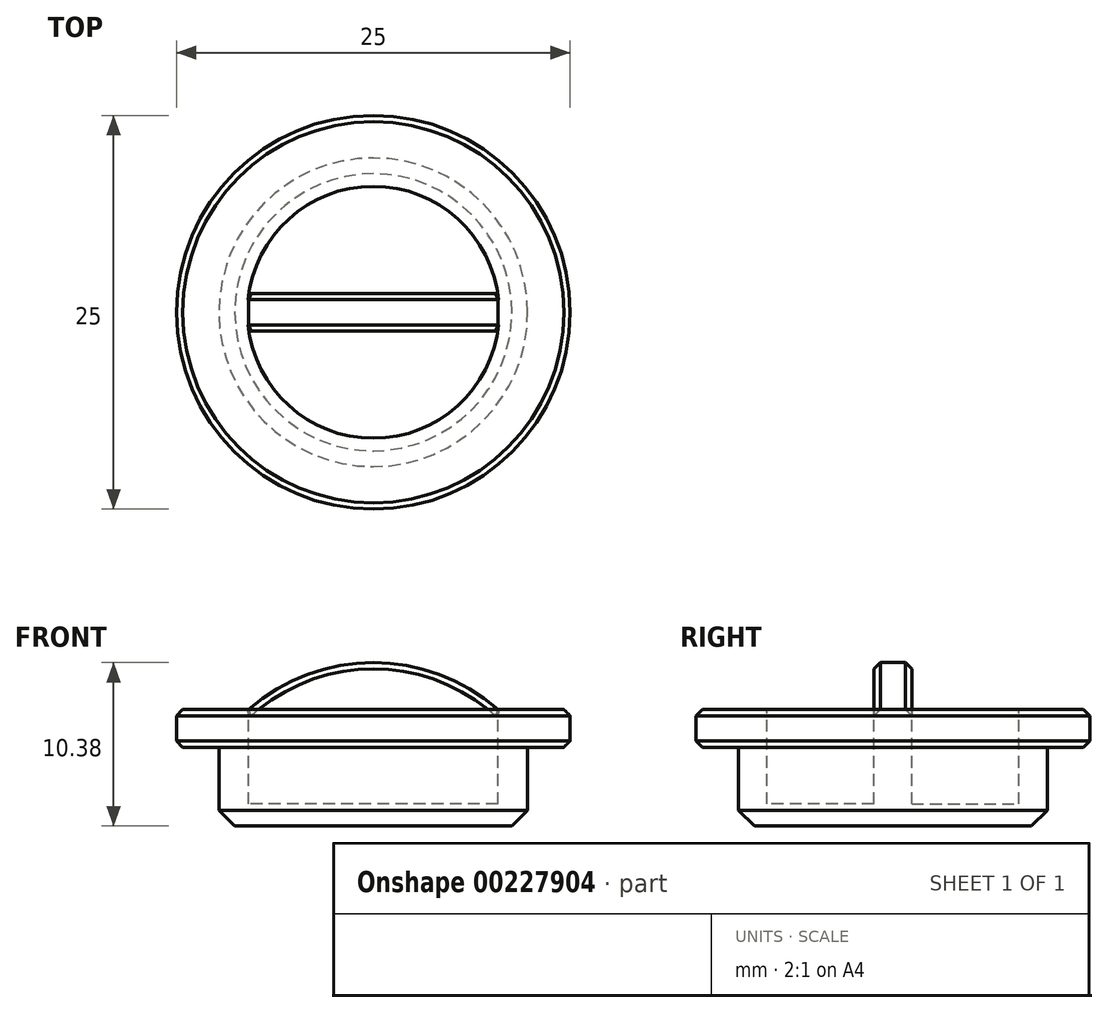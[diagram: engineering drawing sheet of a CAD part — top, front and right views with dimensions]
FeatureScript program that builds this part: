
annotation { "Feature Type Name" : "Feature", "Feature Type Description" : "" }
export const myFeature = defineFeature(function(context is Context, id is Id, definition is map)
    precondition{}
    {
        {
            var Q0;
            Q0=qCreatedBy(makeId("Top.planeOp"),FACE);
            var sketch = newSketch(context, id + "F0", { "sketchPlane" : qUnion([Q0])});
            skCircle(sketch, "E0", {"center": v(0, 0) * mm, "radius": 9.8 * mm});
            skSolve(sketch);
        }
        {
            var Q0;
            Q0=makeQuery(id+"F0.imprint","IMPRINT",FACE,{"disambiguationData":[TD([[makeQuery(id+"F0.imprint","IMPRINT",EDGE,{"derivedFrom":sQuery(id+"F0.wireOp",EDGE,"E0")}),1.0]])]});
            extrude(context, id + "F1", {"entities" : qUnion([Q0]), "depth" : 5 * mm});
        }
        {
            var Q0;
            Q0=makeQuery(id+"F1.opExtrude","CAP_FACE",FACE,{"disambiguationData":[OSD([sQuery(id+"F0.wireOp",EDGE,"E0")])],"isStart":false});
            var sketch = newSketch(context, id + "F2", { "sketchPlane" : qUnion([Q0])});
            skCircle(sketch, "E1", {"center": v(0, 0) * mm, "radius": 12.5 * mm});
            skSolve(sketch);
        }
        {
            var Q0;
            Q0=makeQuery(id+"F2.imprint","IMPRINT",FACE,{"disambiguationData":[TD([[makeQuery(id+"F2.imprint","IMPRINT",EDGE,{"derivedFrom":sQuery(id+"F2.wireOp",EDGE,"E1")}),1.0]])]});
            var Q1;
            Q1=makeQuery(id+"F2.imprint","IMPRINT",FACE,{"disambiguationData":[TD([[makeQuery(id+"F2.imprint","IMPRINT",EDGE,{"derivedFrom":makeQuery(id+"F1.opExtrude","CAP_EDGE",EDGE,{"disambiguationData":[OSD([sQuery(id+"F0.wireOp",EDGE,"E0")])],"isStart":false})}),1.0]])]});
            extrude(context, id + "F3", {"entities" : qUnion([Q0, Q1]), "operationType" : NewBodyOperationType.ADD, "depth" : 2.4 * mm});
        }
        {
            var Q0;
            Q0=makeQuery(id+"F3.opExtrude","CAP_FACE",FACE,{"disambiguationData":[OSD([sQuery(id+"F2.wireOp",EDGE,"E1")])],"isStart":false});
            var sketch = newSketch(context, id + "F4", { "sketchPlane" : qUnion([Q0])});
            skCircle(sketch, "E2", {"center": v(0, 0) * mm, "radius": 8 * mm});
            skSolve(sketch);
        }
        {
            var Q0;
            Q0=makeQuery(id+"F4.imprint","IMPRINT",FACE,{"disambiguationData":[TD([[makeQuery(id+"F4.imprint","IMPRINT",EDGE,{"derivedFrom":sQuery(id+"F4.wireOp",EDGE,"E2")}),1.0]])]});
            extrude(context, id + "F5", {"entities" : qUnion([Q0]), "operationType" : NewBodyOperationType.REMOVE, "oppositeDirection" : true, "depth" : 6 * mm});
        }
        {
            var Q0;
            Q0=makeQuery(id+"F5.boolean.opBoolean","COPY",FACE,{"derivedFrom":makeQuery(id+"F5.opExtrude","CAP_FACE",FACE,{"disambiguationData":[OSD([sQuery(id+"F4.wireOp",EDGE,"E2")])],"isStart":false})});
            var sketch = newSketch(context, id + "F6", { "sketchPlane" : qUnion([Q0])});
            skLineSegment(sketch, "E3.bottom", {"start": v(9, -1.2) * mm, "end": v(-9, -1.2) * mm});
            skLineSegment(sketch, "E3.top", {"start": v(9, 1.2) * mm, "end": v(-9, 1.2) * mm});
            skLineSegment(sketch, "E3.left", {"start": v(9, -1.2) * mm, "end": v(9, 1.2) * mm});
            skLineSegment(sketch, "E3.right", {"start": v(-9, -1.2) * mm, "end": v(-9, 1.2) * mm});
            skPoint(sketch, "E3.middle", {"position": v(0, 0) * mm});
            skSolve(sketch);
        }
        {
            var Q0;
            Q0 = qSketchRegion(id + "F6", true);
            var Q1;
            Q1=makeQuery(id+"F3.opExtrude","CAP_FACE",FACE,{"disambiguationData":[OSD([sQuery(id+"F2.wireOp",EDGE,"E1")])],"isStart":false});
            extrude(context, id + "F7", {"entities" : qUnion([Q0]), "operationType" : NewBodyOperationType.ADD, "endBound" : BoundingType.UP_TO_SURFACE, "endBoundEntityFace" : qUnion([Q1]), "depth" : 25 * mm});
        }
        {
            var Q0;
            Q0=makeQuery(id+"F1.opExtrude","CAP_EDGE",EDGE,{"disambiguationData":[OSD([sQuery(id+"F0.wireOp",EDGE,"E0")])],"isStart":true});
            chamfer(context, id + "F8", {"entities" : qUnion([Q0]), "width" : 1 * mm, "tangentPropagation" : true});
        }
        {
            var Q0;
            Q0=makeQuery(id+"F3.opExtrude","CAP_EDGE",EDGE,{"disambiguationData":[OSD([sQuery(id+"F2.wireOp",EDGE,"E1")])],"isStart":true});
            var Q1;
            Q1=makeQuery(id+"F3.opExtrude","CAP_EDGE",EDGE,{"disambiguationData":[OSD([sQuery(id+"F2.wireOp",EDGE,"E1")])],"isStart":false});
            chamfer(context, id + "F9", {"entities" : qUnion([Q0, Q1]), "width" : 0.4 * mm, "tangentPropagation" : true});
        }
        {
            var Q0;
            Q0=makeQuery(id+"F7.opExtrude","SWEPT_FACE",FACE,{"disambiguationData":[OSD([sQuery(id+"F6.wireOp",EDGE,"E3.bottom")])]});
            var sketch = newSketch(context, id + "F10", { "sketchPlane" : qUnion([Q0])});
            skArc(sketch, "E4", {"start": v(7.9, 7.4) * mm, "mid": v(0, 10.38) * mm, "end": v(-7.9, 7.4) * mm});
            skSolve(sketch);
        }
        {
            var Q0;
            Q0=makeQuery(id+"F10.imprint","IMPRINT",FACE,{"disambiguationData":[TD([[makeQuery(id+"F10.imprint","IMPRINT",EDGE,{"derivedFrom":sQuery(id+"F10.wireOp",EDGE,"E4")}),1.0]])]});
            var Q1;
            Q1=makeQuery(id+"F7.opExtrude","SWEPT_FACE",FACE,{"disambiguationData":[OSD([sQuery(id+"F6.wireOp",EDGE,"E3.top")])]});
            extrude(context, id + "F11", {"entities" : qUnion([Q0]), "operationType" : NewBodyOperationType.ADD, "endBound" : BoundingType.UP_TO_SURFACE, "oppositeDirection" : true, "endBoundEntityFace" : qUnion([Q1]), "depth" : 25 * mm});
        }
        {
            var Q0;
            Q0=makeQuery(id+"F11.opExtrude","CAP_EDGE",EDGE,{"disambiguationData":[OSD([sQuery(id+"F10.wireOp",EDGE,"E4")])],"isStart":true});
            var Q1;
            Q1=makeQuery(id+"F11.opExtrude","CAP_EDGE",EDGE,{"disambiguationData":[OSD([sQuery(id+"F10.wireOp",EDGE,"E4")])],"isStart":false});
            chamfer(context, id + "F12", {"entities" : qUnion([Q0, Q1]), "width" : 0.4 * mm, "tangentPropagation" : true});
        }
        {
            var Q0;
            {var subQ0=sQuery(id+"F10.wireOp",EDGE,"E4");var subQ1=sQuery(id+"F6.wireOp",EDGE,"E3.bottom");var subQ2=makeQuery(id+"F7.opExtrude","SWEPT_FACE",FACE,{"disambiguationData":[OSD([subQ1])]});var subQ3=sQuery(id+"F4.wireOp",EDGE,"E2");var subQ4=makeQuery(id+"F5.boolean.opBoolean","COPY",FACE,{"derivedFrom":makeQuery(id+"F5.opExtrude","SWEPT_FACE",FACE,{"disambiguationData":[OSD([subQ3])]})});Q0=makeQuery(id+"F12.opChamfer","TWEAK_EDGE",EDGE,{"derivedFrom":[makeQuery(id+"F11.boolean.opBoolean","MERGE",VERTEX,{"derivedFrom":[makeQuery(id+"F7.boolean.opBoolean","INTERSECT",VERTEX,{"disambiguationData":[OD(0.0)],"derivedFrom":[subQ4,subQ2]}),makeQuery(id+"F11.opExtrude","CAP_VERTEX",VERTEX,{"disambiguationData":[OSD([subQ3,subQ1,subQ0]),TDD([makeQuery(id+"F10.imprint","INTERSECT",VERTEX,{"derivedFrom":[makeQuery(id+"F7.opExtrude","CAP_EDGE",EDGE,{"disambiguationData":[OSD([subQ1])],"isStart":false}),makeQuery(id+"F7.boolean.opBoolean","INTERSECT",EDGE,{"disambiguationData":[OD(0.0)],"derivedFrom":[subQ4,subQ2]}),subQ0]})])],"isStart":true})]})]});}
            var Q1;
            {var subQ0=sQuery(id+"F4.wireOp",EDGE,"E2");var subQ1=sQuery(id+"F6.wireOp",EDGE,"E3.bottom");Q1=makeQuery(id+"F7.boolean.opBoolean","SPLIT",EDGE,{"disambiguationData":[TD([makeQuery(id+"F7.opExtrude","SWEPT_FACE",FACE,{"disambiguationData":[OSD([subQ1])]})])],"derivedFrom":makeQuery(id+"F5.boolean.opBoolean","COPY",EDGE,{"derivedFrom":makeQuery(id+"F5.opExtrude","CAP_EDGE",EDGE,{"disambiguationData":[OSD([subQ0])],"isStart":true})})});}
            var Q2;
            {var subQ0=sQuery(id+"F10.wireOp",EDGE,"E4");var subQ1=sQuery(id+"F6.wireOp",EDGE,"E3.bottom");var subQ2=makeQuery(id+"F7.opExtrude","SWEPT_FACE",FACE,{"disambiguationData":[OSD([subQ1])]});var subQ3=sQuery(id+"F4.wireOp",EDGE,"E2");var subQ4=makeQuery(id+"F5.boolean.opBoolean","COPY",FACE,{"derivedFrom":makeQuery(id+"F5.opExtrude","SWEPT_FACE",FACE,{"disambiguationData":[OSD([subQ3])]})});Q2=makeQuery(id+"F12.opChamfer","TWEAK_EDGE",EDGE,{"derivedFrom":[makeQuery(id+"F11.boolean.opBoolean","MERGE",VERTEX,{"derivedFrom":[makeQuery(id+"F7.boolean.opBoolean","INTERSECT",VERTEX,{"disambiguationData":[OD(1.0)],"derivedFrom":[subQ4,subQ2]}),makeQuery(id+"F11.opExtrude","CAP_VERTEX",VERTEX,{"disambiguationData":[OSD([subQ3,subQ1,subQ0]),TDD([makeQuery(id+"F10.imprint","INTERSECT",VERTEX,{"derivedFrom":[makeQuery(id+"F7.opExtrude","CAP_EDGE",EDGE,{"disambiguationData":[OSD([subQ1])],"isStart":false}),makeQuery(id+"F7.boolean.opBoolean","INTERSECT",EDGE,{"disambiguationData":[OD(1.0)],"derivedFrom":[subQ4,subQ2]}),subQ0]})])],"isStart":true})]})]});}
            var Q3;
            Q3=makeQuery(id+"F12.opChamfer","TWEAK_EDGE",EDGE,{"derivedFrom":[makeQuery(id+"F11.boolean.opBoolean","MERGE",VERTEX,{"derivedFrom":[makeQuery(id+"F7.boolean.opBoolean","INTERSECT",VERTEX,{"disambiguationData":[OD(0.0)],"derivedFrom":[makeQuery(id+"F5.boolean.opBoolean","COPY",FACE,{"derivedFrom":makeQuery(id+"F5.opExtrude","SWEPT_FACE",FACE,{"disambiguationData":[OSD([sQuery(id+"F4.wireOp",EDGE,"E2")])]})}),makeQuery(id+"F7.opExtrude","SWEPT_FACE",FACE,{"disambiguationData":[OSD([sQuery(id+"F6.wireOp",EDGE,"E3.top")])]})]}),makeQuery(id+"F11.opExtrude","CAP_VERTEX",VERTEX,{"disambiguationData":[OSD([sQuery(id+"F6.wireOp",EDGE,"E3.bottom"),sQuery(id+"F10.wireOp",EDGE,"E4")]),OD(0.0)],"isStart":false})]})]});
            var Q4;
            {var subQ0=sQuery(id+"F4.wireOp",EDGE,"E2");var subQ1=sQuery(id+"F6.wireOp",EDGE,"E3.top");Q4=makeQuery(id+"F7.boolean.opBoolean","SPLIT",EDGE,{"disambiguationData":[TD([makeQuery(id+"F7.opExtrude","SWEPT_FACE",FACE,{"disambiguationData":[OSD([subQ1])]})])],"derivedFrom":makeQuery(id+"F5.boolean.opBoolean","COPY",EDGE,{"derivedFrom":makeQuery(id+"F5.opExtrude","CAP_EDGE",EDGE,{"disambiguationData":[OSD([subQ0])],"isStart":true})})});}
            var Q5;
            Q5=makeQuery(id+"F12.opChamfer","TWEAK_EDGE",EDGE,{"derivedFrom":[makeQuery(id+"F11.boolean.opBoolean","MERGE",VERTEX,{"derivedFrom":[makeQuery(id+"F7.boolean.opBoolean","INTERSECT",VERTEX,{"disambiguationData":[OD(1.0)],"derivedFrom":[makeQuery(id+"F5.boolean.opBoolean","COPY",FACE,{"derivedFrom":makeQuery(id+"F5.opExtrude","SWEPT_FACE",FACE,{"disambiguationData":[OSD([sQuery(id+"F4.wireOp",EDGE,"E2")])]})}),makeQuery(id+"F7.opExtrude","SWEPT_FACE",FACE,{"disambiguationData":[OSD([sQuery(id+"F6.wireOp",EDGE,"E3.top")])]})]}),makeQuery(id+"F11.opExtrude","CAP_VERTEX",VERTEX,{"disambiguationData":[OSD([sQuery(id+"F6.wireOp",EDGE,"E3.bottom"),sQuery(id+"F10.wireOp",EDGE,"E4")]),OD(1.0)],"isStart":false})]})]});
            chamfer(context, id + "F13", {"entities" : qUnion([Q0, Q1, Q2, Q3, Q4, Q5]), "width" : 0.4 * mm, "tangentPropagation" : true});
        }
    });
